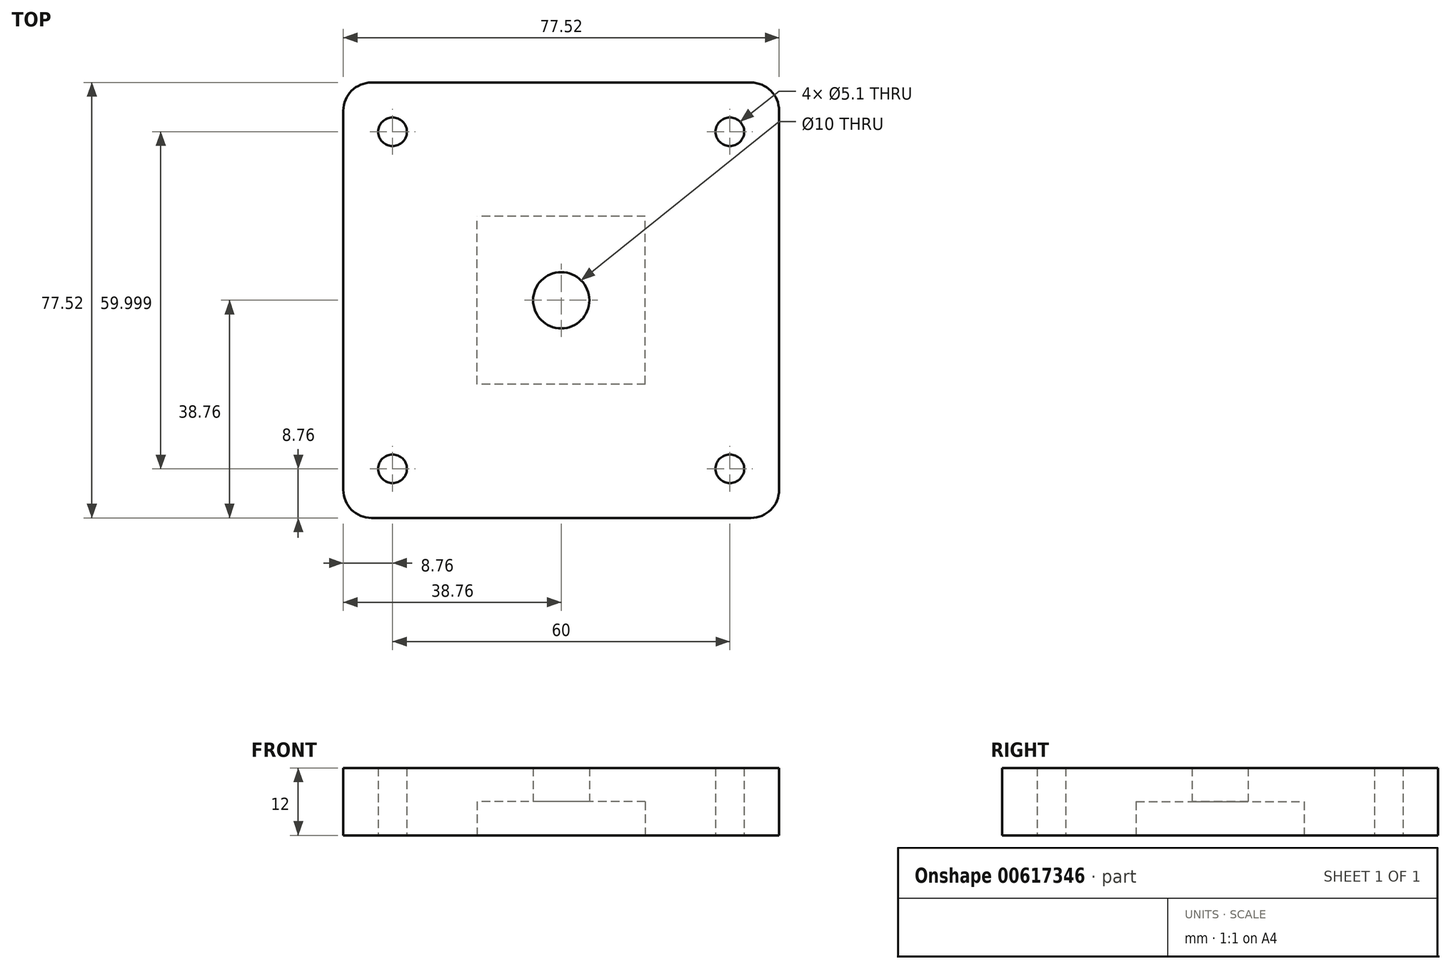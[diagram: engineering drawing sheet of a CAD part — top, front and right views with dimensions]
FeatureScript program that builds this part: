
annotation { "Feature Type Name" : "Feature", "Feature Type Description" : "" }
export const myFeature = defineFeature(function(context is Context, id is Id, definition is map)
    precondition{}
    {
        {
            var Q0;
            Q0=qCreatedBy(makeId("Top.planeOp"),FACE);
            var sketch = newSketch(context, id + "F0", { "sketchPlane" : qUnion([Q0])});
            skLineSegment(sketch, "E0.bottom", {"start": v(38.75, 38.76) * mm, "end": v(-38.76, 38.76) * mm});
            skLineSegment(sketch, "E0.top", {"start": v(38.76, -38.76) * mm, "end": v(-38.76, -38.76) * mm});
            skLineSegment(sketch, "E0.left", {"start": v(38.75, 38.76) * mm, "end": v(38.76, -38.76) * mm});
            skLineSegment(sketch, "E0.right", {"start": v(-38.76, 38.76) * mm, "end": v(-38.75, -38.76) * mm});
            skPoint(sketch, "E0.middle", {"position": v(0, 0) * mm});
            skLineSegment(sketch, "E1.bottom", {"start": v(14.95, -14.95) * mm, "end": v(-14.95, -14.95) * mm});
            skLineSegment(sketch, "E1.top", {"start": v(14.95, 14.95) * mm, "end": v(-14.95, 14.95) * mm});
            skLineSegment(sketch, "E1.left", {"start": v(14.95, -14.95) * mm, "end": v(14.95, 14.95) * mm});
            skLineSegment(sketch, "E1.right", {"start": v(-14.95, -14.95) * mm, "end": v(-14.95, 14.95) * mm});
            skCircle(sketch, "E2", {"center": v(-30, -30) * mm, "radius": 2.55 * mm});
            skCircle(sketch, "E3", {"center": v(30, -30) * mm, "radius": 2.55 * mm});
            skCircle(sketch, "E4", {"center": v(-30, 30) * mm, "radius": 2.55 * mm});
            skCircle(sketch, "E5", {"center": v(30, 30) * mm, "radius": 2.55 * mm});
            skCircle(sketch, "E6", {"center": v(0, 0) * mm, "radius": 5 * mm});
            skSolve(sketch);
        }
        {
            var Q0;
            Q0=makeQuery(id+"F0.imprint","IMPRINT",FACE,{"disambiguationData":[TD([[makeQuery(id+"F0.imprint","IMPRINT",EDGE,{"derivedFrom":sQuery(id+"F0.wireOp",EDGE,"E0.bottom")}),1.0]])]});
            var Q1;
            Q1=makeQuery(id+"F0.imprint","IMPRINT",FACE,{"disambiguationData":[TD([[makeQuery(id+"F0.imprint","IMPRINT",EDGE,{"derivedFrom":sQuery(id+"F0.wireOp",EDGE,"E1.bottom")}),-1.0]])]});
            extrude(context, id + "F1", {"entities" : qUnion([Q0, Q1]), "depth" : 12 * mm, "offsetDistance" : 25 * mm});
        }
        {
            var Q0;
            Q0=makeQuery(id+"F0.imprint","IMPRINT",FACE,{"disambiguationData":[TD([[makeQuery(id+"F0.imprint","IMPRINT",EDGE,{"derivedFrom":sQuery(id+"F0.wireOp",EDGE,"E1.bottom")}),-1.0]])]});
            extrude(context, id + "F2", {"entities" : qUnion([Q0]), "operationType" : NewBodyOperationType.REMOVE, "depth" : 6 * mm, "offsetDistance" : 25 * mm});
        }
        {
            var Q0;
            Q0=makeQuery(id+"F1.opExtrude","SWEPT_EDGE",EDGE,{"disambiguationData":[OSD([sQuery(id+"F0.wireOp",EDGE,"E0.top"),sQuery(id+"F0.wireOp",EDGE,"E0.left")])]});
            var Q1;
            Q1=makeQuery(id+"F1.opExtrude","SWEPT_EDGE",EDGE,{"disambiguationData":[OSD([sQuery(id+"F0.wireOp",EDGE,"E0.top"),sQuery(id+"F0.wireOp",EDGE,"E0.right")])]});
            var Q2;
            Q2=makeQuery(id+"F1.opExtrude","SWEPT_EDGE",EDGE,{"disambiguationData":[OSD([sQuery(id+"F0.wireOp",EDGE,"E0.bottom"),sQuery(id+"F0.wireOp",EDGE,"E0.left")])]});
            var Q3;
            Q3=makeQuery(id+"F1.opExtrude","SWEPT_EDGE",EDGE,{"disambiguationData":[OSD([sQuery(id+"F0.wireOp",EDGE,"E0.bottom"),sQuery(id+"F0.wireOp",EDGE,"E0.right")])]});
            fillet(context, id + "F3", {"entities" : qUnion([Q0, Q1, Q2, Q3]), "radius" : 5 * mm, "tangentPropagation" : true, "allowEdgeOverflow" : false});
        }
    });
